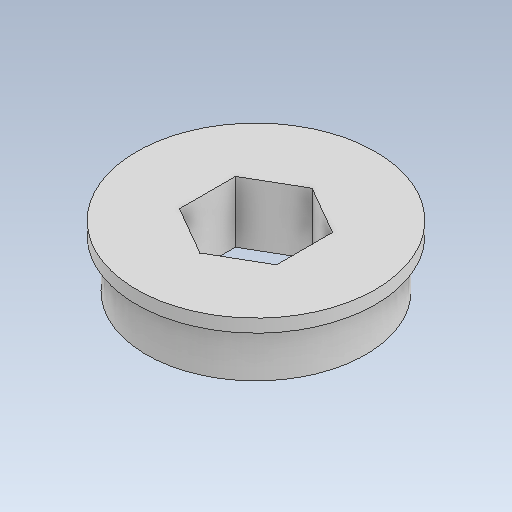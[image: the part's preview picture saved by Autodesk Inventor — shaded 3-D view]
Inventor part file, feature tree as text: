
AUTODESK INVENTOR PART (.ipt)
format: ipt  version: 2023 (Build 270158000, 158)  size: 110,080 bytes
history: native  units: in
note: dims shown in document units (in); Inventor stores cm internally (conversion verified against a paired STEP export)
features: other x3, sketch x2
ambient origin geometry x8: Origin, YZ Plane, XZ Plane, XY Plane, X Axis, Y Axis, Z Axis, Center Point
bodies: Solid1 (feature_tree)
feature tree (5):
  other  "Bearing.ipt"
  other  "Solid1::Bearing.ipt"
  other  "TaggingFeature1"
  sketch  "Sketch1"  dims[d0=0.3937in]
  sketch  "Sketch2"
